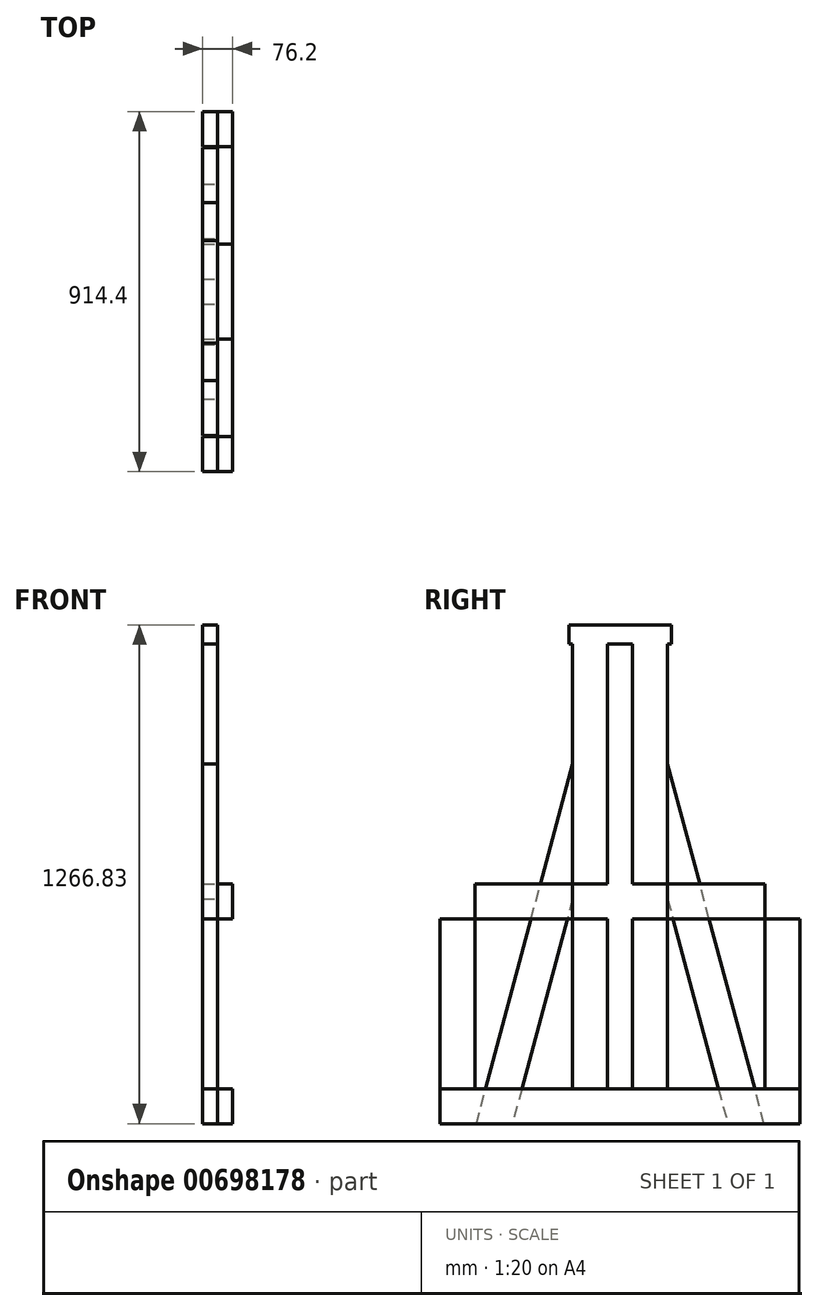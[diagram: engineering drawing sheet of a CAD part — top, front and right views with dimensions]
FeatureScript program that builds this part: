
annotation { "Feature Type Name" : "Feature", "Feature Type Description" : "" }
export const myFeature = defineFeature(function(context is Context, id is Id, definition is map)
    precondition{}
    {
        {
            var Q0;
            Q0=qCreatedBy(makeId("Right.planeOp"),FACE);
            var sketch = newSketch(context, id + "F0", { "sketchPlane" : qUnion([Q0])});
            skLineSegment(sketch, "E0.bottom", {"start": v(-457.2, 0) * mm, "end": v(457.2, 0) * mm});
            skLineSegment(sketch, "E0.top", {"start": v(-457.2, 88.9) * mm, "end": v(457.2, 88.9) * mm});
            skLineSegment(sketch, "E0.left", {"start": v(-457.2, 0) * mm, "end": v(-457.2, 88.9) * mm});
            skLineSegment(sketch, "E0.right", {"start": v(457.2, 0) * mm, "end": v(457.2, 88.9) * mm});
            skLineSegment(sketch, "E1.bottom", {"start": v(31.75, 0) * mm, "end": v(120.65, 0) * mm});
            skLineSegment(sketch, "E1.top", {"start": v(31.75, 1219.2) * mm, "end": v(120.65, 1219.2) * mm});
            skLineSegment(sketch, "E1.left", {"start": v(31.75, 0) * mm, "end": v(31.75, 1219.2) * mm});
            skLineSegment(sketch, "E1.right", {"start": v(120.65, 0) * mm, "end": v(120.65, 1219.2) * mm});
            skLineSegment(sketch, "E2", {"start": v(0, 0) * mm, "end": v(0, 1855.32) * mm, "construction": true});
            skLineSegment(sketch, "E3.bottom", {"start": v(-31.75, 0) * mm, "end": v(-120.65, 0) * mm});
            skLineSegment(sketch, "E3.top", {"start": v(-31.75, 1219.2) * mm, "end": v(-120.65, 1219.2) * mm});
            skLineSegment(sketch, "E3.left", {"start": v(-31.75, 0) * mm, "end": v(-31.75, 1219.2) * mm});
            skLineSegment(sketch, "E3.right", {"start": v(-120.65, 0) * mm, "end": v(-120.65, 1219.2) * mm});
            skLineSegment(sketch, "E4.bottom", {"start": v(-457.2, 0) * mm, "end": v(-368.3, 0) * mm});
            skLineSegment(sketch, "E4.top", {"start": v(-457.2, 609.6) * mm, "end": v(-368.3, 609.6) * mm});
            skLineSegment(sketch, "E4.left", {"start": v(-457.2, 0) * mm, "end": v(-457.2, 609.6) * mm});
            skLineSegment(sketch, "E4.right", {"start": v(-368.3, 0) * mm, "end": v(-368.3, 609.6) * mm});
            skLineSegment(sketch, "E5.bottom", {"start": v(457.2, 0) * mm, "end": v(368.3, 0) * mm});
            skLineSegment(sketch, "E5.top", {"start": v(457.2, 609.6) * mm, "end": v(368.3, 609.6) * mm});
            skLineSegment(sketch, "E5.left", {"start": v(457.2, 0) * mm, "end": v(457.2, 609.6) * mm});
            skLineSegment(sketch, "E5.right", {"start": v(368.3, 0) * mm, "end": v(368.3, 609.6) * mm});
            skLineSegment(sketch, "E6.bottom", {"start": v(-457.2, 609.6) * mm, "end": v(-31.75, 609.6) * mm});
            skLineSegment(sketch, "E6.top", {"start": v(-457.2, 520.7) * mm, "end": v(-31.75, 520.7) * mm});
            skLineSegment(sketch, "E6.left", {"start": v(-457.2, 609.6) * mm, "end": v(-457.2, 520.7) * mm});
            skLineSegment(sketch, "E6.right", {"start": v(-31.75, 609.6) * mm, "end": v(-31.75, 520.7) * mm});
            skLineSegment(sketch, "E7.bottom", {"start": v(457.2, 609.6) * mm, "end": v(31.75, 609.6) * mm});
            skLineSegment(sketch, "E7.top", {"start": v(457.2, 520.7) * mm, "end": v(31.75, 520.7) * mm});
            skLineSegment(sketch, "E7.left", {"start": v(457.2, 609.6) * mm, "end": v(457.2, 520.7) * mm});
            skLineSegment(sketch, "E7.right", {"start": v(31.75, 609.6) * mm, "end": v(31.75, 520.7) * mm});
            skLineSegment(sketch, "E8", {"start": v(-365.84, -0.66) * mm, "end": v(-120.65, 914.4) * mm});
            skLineSegment(sketch, "E9", {"start": v(-120.65, 570.92) * mm, "end": v(-273.63, 0) * mm});
            skLineSegment(sketch, "E10.MirrorCS", {"start": v(365.84, -0.66) * mm, "end": v(120.65, 914.4) * mm});
            skLineSegment(sketch, "E11.MirrorCS", {"start": v(120.65, 570.92) * mm, "end": v(273.63, 0) * mm});
            skLineSegment(sketch, "E12", {"start": v(-120.65, 914.4) * mm, "end": v(-120.65, 570.92) * mm});
            skLineSegment(sketch, "E13", {"start": v(-365.84, -0.66) * mm, "end": v(-273.63, 0) * mm});
            skLineSegment(sketch, "E14", {"start": v(120.65, 570.92) * mm, "end": v(120.65, 914.4) * mm});
            skLineSegment(sketch, "E15", {"start": v(-120.65, 570.92) * mm, "end": v(-120.65, 914.4) * mm});
            skLineSegment(sketch, "E16.MirrorCS", {"start": v(120.65, 914.4) * mm, "end": v(120.65, 570.92) * mm});
            skLineSegment(sketch, "E17.bottom", {"start": v(-130.2, 1219.2) * mm, "end": v(130.15, 1219.2) * mm});
            skLineSegment(sketch, "E17.top", {"start": v(-130.2, 1266.83) * mm, "end": v(130.15, 1266.83) * mm});
            skLineSegment(sketch, "E17.left", {"start": v(-130.2, 1219.2) * mm, "end": v(-130.2, 1266.83) * mm});
            skLineSegment(sketch, "E17.right", {"start": v(130.15, 1219.2) * mm, "end": v(130.15, 1266.83) * mm});
            skSolve(sketch);
        }
        {
            var Q0;
            {var subQ0=sQuery(id+"F0.wireOp",EDGE,"E0.right");Q0=makeQuery(id+"F0.imprint","IMPRINT",FACE,{"disambiguationData":[TD([[makeQuery(id+"F0.imprint","IMPRINT",EDGE,{"derivedFrom":subQ0}),1.0]])]});}
            var Q1;
            {var subQ0=sQuery(id+"F0.wireOp",EDGE,"O3M96ZiU-TQwq-dLFp-mwfa-ZtAqAqBcbGVx.right");var subQ5=sQuery(id+"F0.wireOp",EDGE,"E0.top");var subQ6=makeQuery(id+"F0.imprint","INTERSECT",VERTEX,{"derivedFrom":[subQ5,subQ0]});Q1=makeQuery(id+"F0.imprint","IMPRINT",FACE,{"disambiguationData":[TD([[makeQuery(id+"F0.imprint","IMPRINT",EDGE,{"disambiguationData":[TD([[subQ6,-1.0]])],"derivedFrom":subQ5}),-1.0]])]});}
            var Q2;
            {var subQ0=sQuery(id+"F0.wireOp",EDGE,"E0.left");Q2=makeQuery(id+"F0.imprint","IMPRINT",FACE,{"disambiguationData":[TD([[makeQuery(id+"F0.imprint","IMPRINT",EDGE,{"derivedFrom":subQ0}),-1.0]])]});}
            var Q3;
            {var subQ5=sQuery(id+"F0.wireOp",EDGE,"O3M96ZiU-TQwq-dLFp-mwfa-ZtAqAqBcbGVx.bottom");Q3=makeQuery(id+"F0.imprint","IMPRINT",FACE,{"disambiguationData":[TD([[makeQuery(id+"F0.imprint","IMPRINT",EDGE,{"derivedFrom":subQ5}),1.0]])]});}
            var Q4;
            {var subQ5=sQuery(id+"F0.wireOp",EDGE,"E1.bottom");Q4=makeQuery(id+"F0.imprint","IMPRINT",FACE,{"disambiguationData":[TD([[makeQuery(id+"F0.imprint","IMPRINT",EDGE,{"derivedFrom":subQ5}),1.0]])]});}
            var Q5;
            {var subQ0=sQuery(id+"F0.wireOp",EDGE,"E6.bottom");var subQ1=sQuery(id+"F0.wireOp",EDGE,"E4.right");var subQ2=makeQuery(id+"F0.imprint","INTERSECT",VERTEX,{"derivedFrom":[subQ1,subQ0]});Q5=makeQuery(id+"F0.imprint","IMPRINT",FACE,{"disambiguationData":[TD([[makeQuery(id+"F0.imprint","IMPRINT",EDGE,{"disambiguationData":[TD([[subQ2,1.0]])],"derivedFrom":subQ1}),-1.0]])]});}
            var Q6;
            {var subQ5=sQuery(id+"F0.wireOp",EDGE,"E3.right");var subQ7=sQuery(id+"F0.wireOp",EDGE,"E9");var subQ9=makeQuery(id+"F0.imprint","INTERSECT",VERTEX,{"derivedFrom":[subQ5,subQ7]});Q6=makeQuery(id+"F0.imprint","IMPRINT",FACE,{"disambiguationData":[TD([[makeQuery(id+"F0.imprint","IMPRINT",EDGE,{"disambiguationData":[TD([[subQ9,-1.0]])],"derivedFrom":subQ5}),1.0]])]});}
            var Q7;
            {var subQ0=sQuery(id+"F0.wireOp",EDGE,"E9");var subQ1=sQuery(id+"F0.wireOp",EDGE,"E3.right");var subQ2=makeQuery(id+"F0.imprint","INTERSECT",VERTEX,{"derivedFrom":[subQ1,subQ0]});Q7=makeQuery(id+"F0.imprint","IMPRINT",FACE,{"disambiguationData":[TD([[makeQuery(id+"F0.imprint","IMPRINT",EDGE,{"disambiguationData":[TD([[subQ2,1.0]])],"derivedFrom":subQ1}),1.0]])]});}
            var Q8;
            {var subQ0=sQuery(id+"F0.wireOp",EDGE,"E6.right");Q8=makeQuery(id+"F0.imprint","IMPRINT",FACE,{"disambiguationData":[TD([[makeQuery(id+"F0.imprint","IMPRINT",EDGE,{"derivedFrom":subQ0}),-1.0]])]});}
            var Q9;
            {var subQ5=sQuery(id+"F0.wireOp",EDGE,"E6.left");Q9=makeQuery(id+"F0.imprint","IMPRINT",FACE,{"disambiguationData":[TD([[makeQuery(id+"F0.imprint","IMPRINT",EDGE,{"derivedFrom":subQ5}),1.0]])]});}
            var Q10;
            {var subQ0=sQuery(id+"F0.wireOp",EDGE,"E7.right");Q10=makeQuery(id+"F0.imprint","IMPRINT",FACE,{"disambiguationData":[TD([[makeQuery(id+"F0.imprint","IMPRINT",EDGE,{"derivedFrom":subQ0}),1.0]])]});}
            var Q11;
            {var subQ0=sQuery(id+"F0.wireOp",EDGE,"E11.MirrorCS");var subQ1=sQuery(id+"F0.wireOp",EDGE,"E1.right");var subQ2=makeQuery(id+"F0.imprint","INTERSECT",VERTEX,{"derivedFrom":[subQ1,subQ0]});Q11=makeQuery(id+"F0.imprint","IMPRINT",FACE,{"disambiguationData":[TD([[makeQuery(id+"F0.imprint","IMPRINT",EDGE,{"disambiguationData":[TD([[subQ2,1.0]])],"derivedFrom":subQ1}),-1.0]])]});}
            var Q12;
            {var subQ5=sQuery(id+"F0.wireOp",EDGE,"E11.MirrorCS");var subQ7=sQuery(id+"F0.wireOp",EDGE,"E1.right");var subQ9=makeQuery(id+"F0.imprint","INTERSECT",VERTEX,{"derivedFrom":[subQ7,subQ5]});Q12=makeQuery(id+"F0.imprint","IMPRINT",FACE,{"disambiguationData":[TD([[makeQuery(id+"F0.imprint","IMPRINT",EDGE,{"disambiguationData":[TD([[subQ9,-1.0]])],"derivedFrom":subQ7}),-1.0]])]});}
            var Q13;
            {var subQ0=sQuery(id+"F0.wireOp",EDGE,"E7.bottom");var subQ1=sQuery(id+"F0.wireOp",EDGE,"E5.right");var subQ2=makeQuery(id+"F0.imprint","INTERSECT",VERTEX,{"derivedFrom":[subQ1,subQ0]});Q13=makeQuery(id+"F0.imprint","IMPRINT",FACE,{"disambiguationData":[TD([[makeQuery(id+"F0.imprint","IMPRINT",EDGE,{"disambiguationData":[TD([[subQ2,1.0]])],"derivedFrom":subQ1}),1.0]])]});}
            var Q14;
            {var subQ5=sQuery(id+"F0.wireOp",EDGE,"E7.left");Q14=makeQuery(id+"F0.imprint","IMPRINT",FACE,{"disambiguationData":[TD([[makeQuery(id+"F0.imprint","IMPRINT",EDGE,{"derivedFrom":subQ5}),-1.0]])]});}
            var Q15;
            {var subQ0=sQuery(id+"F0.wireOp",EDGE,"E8");var subQ1=sQuery(id+"F0.wireOp",EDGE,"E6.bottom");var subQ2=makeQuery(id+"F0.imprint","INTERSECT",VERTEX,{"derivedFrom":[subQ1,subQ0]});Q15=makeQuery(id+"F0.imprint","IMPRINT",FACE,{"disambiguationData":[TD([[makeQuery(id+"F0.imprint","IMPRINT",EDGE,{"disambiguationData":[TD([[subQ2,-1.0]])],"derivedFrom":subQ1}),-1.0]])]});}
            var Q16;
            {var subQ5=sQuery(id+"F0.wireOp",EDGE,"E10.MirrorCS");var subQ6=sQuery(id+"F0.wireOp",EDGE,"E7.bottom");var subQ7=makeQuery(id+"F0.imprint","INTERSECT",VERTEX,{"derivedFrom":[subQ6,subQ5]});Q16=makeQuery(id+"F0.imprint","IMPRINT",FACE,{"disambiguationData":[TD([[makeQuery(id+"F0.imprint","IMPRINT",EDGE,{"disambiguationData":[TD([[subQ7,-1.0]])],"derivedFrom":subQ6}),1.0]])]});}
            extrude(context, id + "F1", {"entities" : qUnion([Q0, Q1, Q2, Q3, Q4, Q5, Q6, Q7, Q8, Q9, Q10, Q11, Q12, Q13, Q14, Q15, Q16]), "depth" : 38.1 * mm, "offsetDistance" : 25.4 * mm});
        }
        {
            var Q0;
            {var subQ5=sQuery(id+"F0.wireOp",EDGE,"E3.top");Q0=makeQuery(id+"F0.imprint","IMPRINT",FACE,{"disambiguationData":[TD([[makeQuery(id+"F0.imprint","IMPRINT",EDGE,{"derivedFrom":subQ5}),1.0]])]});}
            var Q1;
            {var subQ5=sQuery(id+"F0.wireOp",EDGE,"E1.top");Q1=makeQuery(id+"F0.imprint","IMPRINT",FACE,{"disambiguationData":[TD([[makeQuery(id+"F0.imprint","IMPRINT",EDGE,{"derivedFrom":subQ5}),-1.0]])]});}
            var Q2;
            {var subQ5=sQuery(id+"F0.wireOp",EDGE,"E3.bottom");Q2=makeQuery(id+"F0.imprint","IMPRINT",FACE,{"disambiguationData":[TD([[makeQuery(id+"F0.imprint","IMPRINT",EDGE,{"derivedFrom":subQ5}),-1.0]])]});}
            var Q3;
            {var subQ5=sQuery(id+"F0.wireOp",EDGE,"E1.bottom");Q3=makeQuery(id+"F0.imprint","IMPRINT",FACE,{"disambiguationData":[TD([[makeQuery(id+"F0.imprint","IMPRINT",EDGE,{"derivedFrom":subQ5}),1.0]])]});}
            var Q4;
            {var subQ0=sQuery(id+"F0.wireOp",EDGE,"E6.right");Q4=makeQuery(id+"F0.imprint","IMPRINT",FACE,{"disambiguationData":[TD([[makeQuery(id+"F0.imprint","IMPRINT",EDGE,{"derivedFrom":subQ0}),-1.0]])]});}
            var Q5;
            {var subQ0=sQuery(id+"F0.wireOp",EDGE,"E3.left");var subQ1=sQuery(id+"F0.wireOp",EDGE,"E0.top");var subQ2=makeQuery(id+"F0.imprint","INTERSECT",VERTEX,{"derivedFrom":[subQ1,subQ0]});Q5=makeQuery(id+"F0.imprint","IMPRINT",FACE,{"disambiguationData":[TD([[makeQuery(id+"F0.imprint","IMPRINT",EDGE,{"disambiguationData":[TD([[subQ2,1.0]])],"derivedFrom":subQ1}),1.0]])]});}
            var Q6;
            {var subQ0=sQuery(id+"F0.wireOp",EDGE,"E1.left");var subQ1=sQuery(id+"F0.wireOp",EDGE,"E0.top");var subQ2=makeQuery(id+"F0.imprint","INTERSECT",VERTEX,{"derivedFrom":[subQ1,subQ0]});Q6=makeQuery(id+"F0.imprint","IMPRINT",FACE,{"disambiguationData":[TD([[makeQuery(id+"F0.imprint","IMPRINT",EDGE,{"disambiguationData":[TD([[subQ2,-1.0]])],"derivedFrom":subQ1}),1.0]])]});}
            var Q7;
            {var subQ0=sQuery(id+"F0.wireOp",EDGE,"E7.right");Q7=makeQuery(id+"F0.imprint","IMPRINT",FACE,{"disambiguationData":[TD([[makeQuery(id+"F0.imprint","IMPRINT",EDGE,{"derivedFrom":subQ0}),1.0]])]});}
            var Q8;
            {var subQ0=sQuery(id+"F0.wireOp",EDGE,"E4.left");var subQ1=sQuery(id+"F0.wireOp",EDGE,"E0.top");var subQ2=makeQuery(id+"F0.imprint","INTERSECT",VERTEX,{"derivedFrom":[subQ1,subQ0]});Q8=makeQuery(id+"F0.imprint","IMPRINT",FACE,{"disambiguationData":[TD([[makeQuery(id+"F0.imprint","IMPRINT",EDGE,{"disambiguationData":[TD([[subQ2,-1.0]])],"derivedFrom":subQ1}),1.0]])]});}
            var Q9;
            {var subQ5=sQuery(id+"F0.wireOp",EDGE,"E6.left");Q9=makeQuery(id+"F0.imprint","IMPRINT",FACE,{"disambiguationData":[TD([[makeQuery(id+"F0.imprint","IMPRINT",EDGE,{"derivedFrom":subQ5}),1.0]])]});}
            var Q10;
            {var subQ5=sQuery(id+"F0.wireOp",EDGE,"E4.bottom");Q10=makeQuery(id+"F0.imprint","IMPRINT",FACE,{"disambiguationData":[TD([[makeQuery(id+"F0.imprint","IMPRINT",EDGE,{"derivedFrom":subQ5}),1.0]])]});}
            var Q11;
            {var subQ5=sQuery(id+"F0.wireOp",EDGE,"E7.left");Q11=makeQuery(id+"F0.imprint","IMPRINT",FACE,{"disambiguationData":[TD([[makeQuery(id+"F0.imprint","IMPRINT",EDGE,{"derivedFrom":subQ5}),-1.0]])]});}
            var Q12;
            {var subQ0=sQuery(id+"F0.wireOp",EDGE,"E5.left");var subQ1=sQuery(id+"F0.wireOp",EDGE,"E0.top");var subQ2=makeQuery(id+"F0.imprint","INTERSECT",VERTEX,{"derivedFrom":[subQ1,subQ0]});Q12=makeQuery(id+"F0.imprint","IMPRINT",FACE,{"disambiguationData":[TD([[makeQuery(id+"F0.imprint","IMPRINT",EDGE,{"disambiguationData":[TD([[subQ2,1.0]])],"derivedFrom":subQ1}),1.0]])]});}
            var Q13;
            {var subQ5=sQuery(id+"F0.wireOp",EDGE,"E5.bottom");Q13=makeQuery(id+"F0.imprint","IMPRINT",FACE,{"disambiguationData":[TD([[makeQuery(id+"F0.imprint","IMPRINT",EDGE,{"derivedFrom":subQ5}),-1.0]])]});}
            var Q14;
            {var subQ0=sQuery(id+"F0.wireOp",EDGE,"E8");var subQ1=sQuery(id+"F0.wireOp",EDGE,"E3.right");var subQ2=makeQuery(id+"F0.imprint","INTERSECT",VERTEX,{"derivedFrom":[subQ1,subQ0]});Q14=makeQuery(id+"F0.imprint","IMPRINT",FACE,{"disambiguationData":[TD([[makeQuery(id+"F0.imprint","IMPRINT",EDGE,{"disambiguationData":[TD([[subQ2,1.0]])],"derivedFrom":subQ1}),1.0]])]});}
            var Q15;
            {var subQ5=sQuery(id+"F0.wireOp",EDGE,"E3.right");var subQ7=sQuery(id+"F0.wireOp",EDGE,"E9");var subQ9=makeQuery(id+"F0.imprint","INTERSECT",VERTEX,{"derivedFrom":[subQ5,subQ7]});Q15=makeQuery(id+"F0.imprint","IMPRINT",FACE,{"disambiguationData":[TD([[makeQuery(id+"F0.imprint","IMPRINT",EDGE,{"disambiguationData":[TD([[subQ9,-1.0]])],"derivedFrom":subQ5}),1.0]])]});}
            var Q16;
            {var subQ0=sQuery(id+"F0.wireOp",EDGE,"E10.MirrorCS");var subQ1=sQuery(id+"F0.wireOp",EDGE,"E1.right");var subQ2=makeQuery(id+"F0.imprint","INTERSECT",VERTEX,{"derivedFrom":[subQ1,subQ0]});Q16=makeQuery(id+"F0.imprint","IMPRINT",FACE,{"disambiguationData":[TD([[makeQuery(id+"F0.imprint","IMPRINT",EDGE,{"disambiguationData":[TD([[subQ2,1.0]])],"derivedFrom":subQ1}),-1.0]])]});}
            var Q17;
            {var subQ5=sQuery(id+"F0.wireOp",EDGE,"E11.MirrorCS");var subQ7=sQuery(id+"F0.wireOp",EDGE,"E1.right");var subQ9=makeQuery(id+"F0.imprint","INTERSECT",VERTEX,{"derivedFrom":[subQ7,subQ5]});Q17=makeQuery(id+"F0.imprint","IMPRINT",FACE,{"disambiguationData":[TD([[makeQuery(id+"F0.imprint","IMPRINT",EDGE,{"disambiguationData":[TD([[subQ9,-1.0]])],"derivedFrom":subQ7}),-1.0]])]});}
            var Q18;
            {var subQ5=sQuery(id+"F0.wireOp",EDGE,"E17.bottom");var subQ7=sQuery(id+"F0.wireOp",EDGE,"E3.left");var subQ9=makeQuery(id+"F0.imprint","INTERSECT",VERTEX,{"derivedFrom":[subQ7,subQ5]});Q18=makeQuery(id+"F0.imprint","IMPRINT",FACE,{"disambiguationData":[TD([[makeQuery(id+"F0.imprint","IMPRINT",EDGE,{"disambiguationData":[TD([[subQ9,1.0]])],"derivedFrom":subQ5}),-1.0]])]});}
            var Q19;
            {var subQ1=sQuery(id+"F0.wireOp",EDGE,"E1.left");var subQ5=sQuery(id+"F0.wireOp",EDGE,"E17.bottom");var subQ9=makeQuery(id+"F0.imprint","INTERSECT",VERTEX,{"derivedFrom":[subQ1,subQ5]});Q19=makeQuery(id+"F0.imprint","IMPRINT",FACE,{"disambiguationData":[TD([[makeQuery(id+"F0.imprint","IMPRINT",EDGE,{"disambiguationData":[TD([[subQ9,-1.0]])],"derivedFrom":subQ5}),-1.0]])]});}
            var Q20;
            Q20=makeQuery(id+"F0.imprint","IMPRINT",FACE,{"disambiguationData":[TD([[makeQuery(id+"F0.imprint","IMPRINT",EDGE,{"derivedFrom":sQuery(id+"F0.wireOp",EDGE,"E17.top")}),-1.0]])]});
            var Q21;
            {var subQ5=sQuery(id+"F0.wireOp",EDGE,"E17.bottom");var subQ7=sQuery(id+"F0.wireOp",EDGE,"E3.left");var subQ9=makeQuery(id+"F0.imprint","INTERSECT",VERTEX,{"derivedFrom":[subQ7,subQ5]});Q21=makeQuery(id+"F0.imprint","IMPRINT",FACE,{"disambiguationData":[TD([[makeQuery(id+"F0.imprint","IMPRINT",EDGE,{"disambiguationData":[TD([[subQ9,1.0]])],"derivedFrom":subQ5}),-1.0]])]});}
            var Q22;
            {var subQ1=sQuery(id+"F0.wireOp",EDGE,"E1.left");var subQ5=sQuery(id+"F0.wireOp",EDGE,"E17.bottom");var subQ9=makeQuery(id+"F0.imprint","INTERSECT",VERTEX,{"derivedFrom":[subQ1,subQ5]});Q22=makeQuery(id+"F0.imprint","IMPRINT",FACE,{"disambiguationData":[TD([[makeQuery(id+"F0.imprint","IMPRINT",EDGE,{"disambiguationData":[TD([[subQ9,-1.0]])],"derivedFrom":subQ5}),-1.0]])]});}
            extrude(context, id + "F2", {"entities" : qUnion([Q0, Q1, Q2, Q3, Q4, Q5, Q6, Q7, Q8, Q9, Q10, Q11, Q12, Q13, Q14, Q15, Q16, Q17, Q18, Q19, Q20, Q21, Q22]), "oppositeDirection" : true, "depth" : 38.1 * mm, "offsetDistance" : 25.4 * mm});
        }
        {
            var Q0;
            {var subQ0=sQuery(id+"F0.wireOp",EDGE,"E8");var subQ1=sQuery(id+"F0.wireOp",EDGE,"E6.bottom");var subQ2=makeQuery(id+"F0.imprint","INTERSECT",VERTEX,{"derivedFrom":[subQ1,subQ0]});Q0=makeQuery(id+"F0.imprint","IMPRINT",FACE,{"disambiguationData":[TD([[makeQuery(id+"F0.imprint","IMPRINT",EDGE,{"disambiguationData":[TD([[subQ2,-1.0]])],"derivedFrom":subQ1}),1.0]])]});}
            var Q1;
            {var subQ0=sQuery(id+"F0.wireOp",EDGE,"E8");var subQ1=sQuery(id+"F0.wireOp",EDGE,"E6.bottom");var subQ2=makeQuery(id+"F0.imprint","INTERSECT",VERTEX,{"derivedFrom":[subQ1,subQ0]});Q1=makeQuery(id+"F0.imprint","IMPRINT",FACE,{"disambiguationData":[TD([[makeQuery(id+"F0.imprint","IMPRINT",EDGE,{"disambiguationData":[TD([[subQ2,-1.0]])],"derivedFrom":subQ1}),-1.0]])]});}
            var Q2;
            {var subQ0=sQuery(id+"F0.wireOp",EDGE,"E8");var subQ1=sQuery(id+"F0.wireOp",EDGE,"E0.top");var subQ2=makeQuery(id+"F0.imprint","INTERSECT",VERTEX,{"derivedFrom":[subQ1,subQ0]});Q2=makeQuery(id+"F0.imprint","IMPRINT",FACE,{"disambiguationData":[TD([[makeQuery(id+"F0.imprint","IMPRINT",EDGE,{"disambiguationData":[TD([[subQ2,-1.0]])],"derivedFrom":subQ1}),1.0]])]});}
            var Q3;
            {var subQ0=sQuery(id+"F0.wireOp",EDGE,"E10.MirrorCS");var subQ1=sQuery(id+"F0.wireOp",EDGE,"E7.bottom");var subQ2=makeQuery(id+"F0.imprint","INTERSECT",VERTEX,{"derivedFrom":[subQ1,subQ0]});Q3=makeQuery(id+"F0.imprint","IMPRINT",FACE,{"disambiguationData":[TD([[makeQuery(id+"F0.imprint","IMPRINT",EDGE,{"disambiguationData":[TD([[subQ2,-1.0]])],"derivedFrom":subQ1}),-1.0]])]});}
            var Q4;
            {var subQ5=sQuery(id+"F0.wireOp",EDGE,"E10.MirrorCS");var subQ6=sQuery(id+"F0.wireOp",EDGE,"E7.bottom");var subQ7=makeQuery(id+"F0.imprint","INTERSECT",VERTEX,{"derivedFrom":[subQ6,subQ5]});Q4=makeQuery(id+"F0.imprint","IMPRINT",FACE,{"disambiguationData":[TD([[makeQuery(id+"F0.imprint","IMPRINT",EDGE,{"disambiguationData":[TD([[subQ7,-1.0]])],"derivedFrom":subQ6}),1.0]])]});}
            var Q5;
            {var subQ0=sQuery(id+"F0.wireOp",EDGE,"E11.MirrorCS");var subQ1=sQuery(id+"F0.wireOp",EDGE,"E0.top");var subQ2=makeQuery(id+"F0.imprint","INTERSECT",VERTEX,{"derivedFrom":[subQ1,subQ0]});Q5=makeQuery(id+"F0.imprint","IMPRINT",FACE,{"disambiguationData":[TD([[makeQuery(id+"F0.imprint","IMPRINT",EDGE,{"disambiguationData":[TD([[subQ2,-1.0]])],"derivedFrom":subQ1}),1.0]])]});}
            var Q6;
            {var subQ3=sQuery(id+"F0.wireOp",EDGE,"E8");var subQ5=sQuery(id+"F0.wireOp",EDGE,"E0.top");var subQ6=makeQuery(id+"F0.imprint","INTERSECT",VERTEX,{"derivedFrom":[subQ5,subQ3]});Q6=makeQuery(id+"F0.imprint","IMPRINT",FACE,{"disambiguationData":[TD([[makeQuery(id+"F0.imprint","IMPRINT",EDGE,{"disambiguationData":[TD([[subQ6,-1.0]])],"derivedFrom":subQ5}),-1.0]])]});}
            var Q7;
            {var subQ0=sQuery(id+"F0.wireOp",EDGE,"E11.MirrorCS");var subQ1=sQuery(id+"F0.wireOp",EDGE,"E0.bottom");var subQ2=makeQuery(id+"F0.imprint","INTERSECT",VERTEX,{"derivedFrom":[subQ1,subQ0]});Q7=makeQuery(id+"F0.imprint","IMPRINT",FACE,{"disambiguationData":[TD([[makeQuery(id+"F0.imprint","IMPRINT",EDGE,{"disambiguationData":[TD([[subQ2,-1.0]])],"derivedFrom":subQ1}),1.0]])]});}
            extrude(context, id + "F3", {"entities" : qUnion([Q0, Q1, Q2, Q3, Q4, Q5, Q6, Q7]), "oppositeDirection" : true, "depth" : 38.1 * mm, "offsetDistance" : 25.4 * mm});
        }
    });
